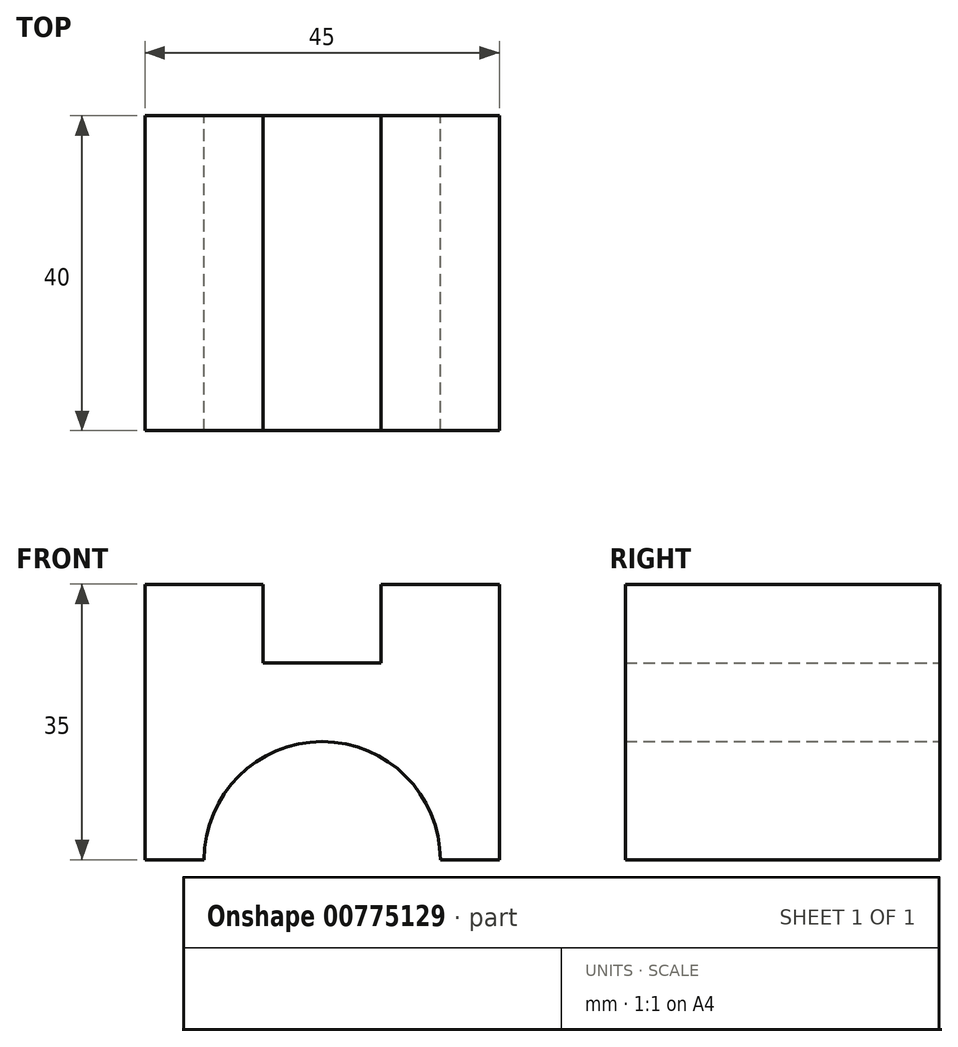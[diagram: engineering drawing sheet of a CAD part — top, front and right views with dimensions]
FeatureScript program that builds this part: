
annotation { "Feature Type Name" : "Feature", "Feature Type Description" : "" }
export const myFeature = defineFeature(function(context is Context, id is Id, definition is map)
    precondition{}
    {
        {
            var Q0;
            Q0=qCreatedBy(makeId("Front.planeOp"),FACE);
            var sketch = newSketch(context, id + "F0", { "sketchPlane" : qUnion([Q0])});
            skLineSegment(sketch, "E0.bottom", {"start": v(-8.5, 26.43) * mm, "end": v(6.5, 26.43) * mm});
            skLineSegment(sketch, "E0.top", {"start": v(-8.5, -8.57) * mm, "end": v(-1, -8.57) * mm});
            skLineSegment(sketch, "E0.left", {"start": v(-8.5, 26.43) * mm, "end": v(-8.5, -8.57) * mm});
            skLineSegment(sketch, "E0.right", {"start": v(36.5, 26.43) * mm, "end": v(36.5, -8.57) * mm});
            skPoint(sketch, "E1", {"position": v(6.5, 26.43) * mm});
            skPoint(sketch, "E2", {"position": v(21.5, 26.43) * mm});
            skLineSegment(sketch, "E3.top", {"start": v(6.5, 16.43) * mm, "end": v(21.5, 16.43) * mm});
            skLineSegment(sketch, "E3.left", {"start": v(6.5, 26.43) * mm, "end": v(6.5, 16.43) * mm});
            skLineSegment(sketch, "E3.right", {"start": v(21.5, 26.43) * mm, "end": v(21.5, 16.43) * mm});
            skLineSegment(sketch, "E4.trimOffspring", {"start": v(21.5, 26.43) * mm, "end": v(36.5, 26.43) * mm});
            skArc(sketch, "E5", {"start": v(29, -8.57) * mm, "mid": v(14, 6.43) * mm, "end": v(-1, -8.57) * mm});
            skLineSegment(sketch, "E6.trimOffspring", {"start": v(29, -8.57) * mm, "end": v(36.5, -8.57) * mm});
            skSolve(sketch);
        }
        {
            var Q0;
            Q0=makeQuery(id+"F0.imprint","IMPRINT",FACE,{"disambiguationData":[TD([[makeQuery(id+"F0.imprint","IMPRINT",EDGE,{"derivedFrom":sQuery(id+"F0.wireOp",EDGE,"E0.bottom")}),-1.0]])]});
            extrude(context, id + "F1", {"entities" : qUnion([Q0]), "depth" : 40 * mm, "offsetDistance" : 25 * mm});
        }
    });
